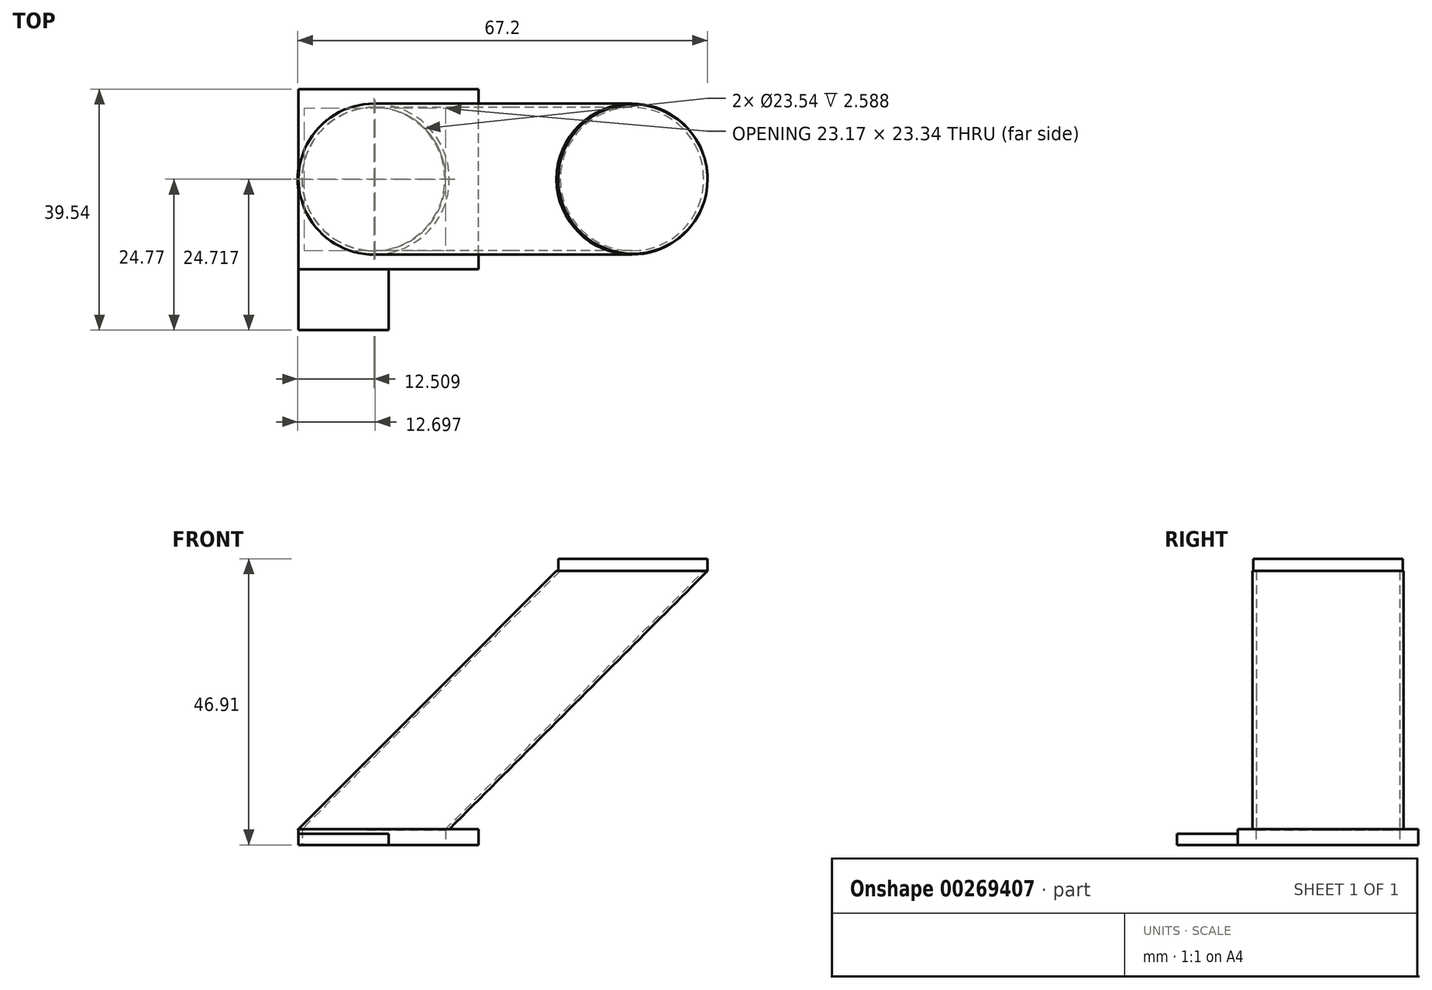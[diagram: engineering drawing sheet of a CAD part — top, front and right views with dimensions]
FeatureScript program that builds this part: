
annotation { "Feature Type Name" : "Feature", "Feature Type Description" : "" }
export const myFeature = defineFeature(function(context is Context, id is Id, definition is map)
    precondition{}
    {
        {
            var Q0;
            Q0=qCreatedBy(makeId("Top.planeOp"),FACE);
            var sketch = newSketch(context, id + "F0", { "sketchPlane" : qUnion([Q0])});
            skLineSegment(sketch, "E0.bottom", {"start": v(14.77, -14.77) * mm, "end": v(-14.77, -14.77) * mm});
            skLineSegment(sketch, "E0.top", {"start": v(14.77, 14.77) * mm, "end": v(-14.77, 14.77) * mm});
            skLineSegment(sketch, "E0.left", {"start": v(14.77, -14.77) * mm, "end": v(14.77, 14.77) * mm});
            skLineSegment(sketch, "E0.right", {"start": v(-14.77, -14.77) * mm, "end": v(-14.77, 14.77) * mm});
            skPoint(sketch, "E0.middle", {"position": v(0, 0) * mm});
            skLineSegment(sketch, "E1", {"start": v(14.77, 0) * mm, "end": v(9.37, 0) * mm});
            skPoint(sketch, "E1.endSnap0", {"position": v(14.77, 0) * mm});
            skCircle(sketch, "E2", {"center": v(-2.4, 0) * mm, "radius": 11.77 * mm});
            skLineSegment(sketch, "E3", {"start": v(14.77, -14.77) * mm, "end": v(0, -14.77) * mm});
            skLineSegment(sketch, "E4", {"start": v(0, 14.77) * mm, "end": v(-14.77, 14.77) * mm});
            skLineSegment(sketch, "E5", {"start": v(-14.77, -14.77) * mm, "end": v(-14.77, -24.77) * mm});
            skLineSegment(sketch, "E6", {"start": v(-14.77, -24.77) * mm, "end": v(0, -24.77) * mm});
            skLineSegment(sketch, "E7", {"start": v(0, -24.77) * mm, "end": v(0, -14.77) * mm});
            skSolve(sketch);
        }
        {
            var Q0;
            {var subQ3=sQuery(id+"F0.wireOp",EDGE,"E0.bottom");Q0=makeQuery(id+"F0.imprint","IMPRINT",FACE,{"disambiguationData":[TD([[makeQuery(id+"F0.imprint","IMPRINT",EDGE,{"derivedFrom":subQ3}),-1.0]])]});}
            extrude(context, id + "F1", {"entities" : qUnion([Q0]), "depth" : 2.6 * mm});
        }
        {
            var Q0;
            Q0=makeQuery(id+"F1.opExtrude","CAP_FACE",FACE,{"disambiguationData":[OSD([sQuery(id+"F0.wireOp",EDGE,"E0.bottom"),sQuery(id+"F0.wireOp",EDGE,"E0.top"),sQuery(id+"F0.wireOp",EDGE,"E0.left"),sQuery(id+"F0.wireOp",EDGE,"E0.right"),sQuery(id+"F0.wireOp",EDGE,"E2")])],"isStart":false});
            var sketch = newSketch(context, id + "F2", { "sketchPlane" : qUnion([Q0])});
            skCircle(sketch, "E8", {"center": v(-2.4, 0) * mm, "radius": 12.37 * mm});
            skCircle(sketch, "E9", {"center": v(-2.4, 0) * mm, "radius": 11.76 * mm});
            skSolve(sketch);
        }
        {
            var Q0;
            Q0=makeQuery(id+"F0.imprint","IMPRINT",FACE,{"disambiguationData":[TD([[makeQuery(id+"F0.imprint","IMPRINT",EDGE,{"derivedFrom":sQuery(id+"F0.wireOp",EDGE,"E0.bottom")}),1.0]])]});
            extrude(context, id + "F3", {"entities" : qUnion([Q0]), "operationType" : NewBodyOperationType.ADD, "depth" : 1.8 * mm});
        }
        {
            var Q0;
            Q0=qCreatedBy(makeId("Front.planeOp"),FACE);
            var sketch = newSketch(context, id + "F4", { "sketchPlane" : qUnion([Q0])});
            skLineSegment(sketch, "E10", {"start": v(-2.27, 2.46) * mm, "end": v(20.39, 25.11) * mm});
            skLineSegment(sketch, "E11", {"start": v(20.39, 25.11) * mm, "end": v(40.18, 44.91) * mm});
            skSolve(sketch);
        }
        {
            var Q0;
            Q0 = qSketchRegion(id + "F2", true);
            var Q1;
            Q1=sQuery(id+"F4.wireOp",EDGE,"E10");
            var Q2;
            Q2=sQuery(id+"F4.wireOp",EDGE,"E11");
            sweep(context, id + "F5", {"operationType" : NewBodyOperationType.ADD, "profiles" : qUnion([Q0]), "path" : qUnion([Q1, Q2])});
        }
        {
            var Q0;
            Q0=makeQuery(id+"F5.opSweep","CAP_FACE",FACE,{"disambiguationData":[OSD([sQuery(id+"F2.wireOp",EDGE,"E8"),sQuery(id+"F2.wireOp",EDGE,"E9"),sQuery(id+"F4.wireOp",VERTEX,"E11.end")])],"isStart":false});
            var sketch = newSketch(context, id + "F6", { "sketchPlane" : qUnion([Q0])});
            skCircle(sketch, "E12", {"center": v(40.05, 0) * mm, "radius": 12.24 * mm});
            skSolve(sketch);
        }
        {
            var Q0;
            Q0 = qSketchRegion(id + "F6", true);
            extrude(context, id + "F7", {"entities" : qUnion([Q0]), "operationType" : NewBodyOperationType.ADD, "depth" : 2 * mm});
        }
        {
            var Q0;
            Q0=makeQuery(id+"F1.opExtrude","SWEPT_BODY",BODY,{"disambiguationData":[OSD([sQuery(id+"F0.wireOp",EDGE,"E0.bottom"),sQuery(id+"F0.wireOp",EDGE,"E0.top"),sQuery(id+"F0.wireOp",EDGE,"E0.left"),sQuery(id+"F0.wireOp",EDGE,"E0.right"),sQuery(id+"F0.wireOp",EDGE,"E2"),sQuery(id+"F0.wireOp",EDGE,"E3"),sQuery(id+"F0.wireOp",EDGE,"E4")])]});
            transform(context, id + "F8", {"entities" : qUnion([Q0]), "transformType" : TransformType.TRANSLATION_3D, "dx" : 0 * mm, "dy" : 0 * mm, "dz" : 0 * mm, "makeCopy" : true});
        }
    });
